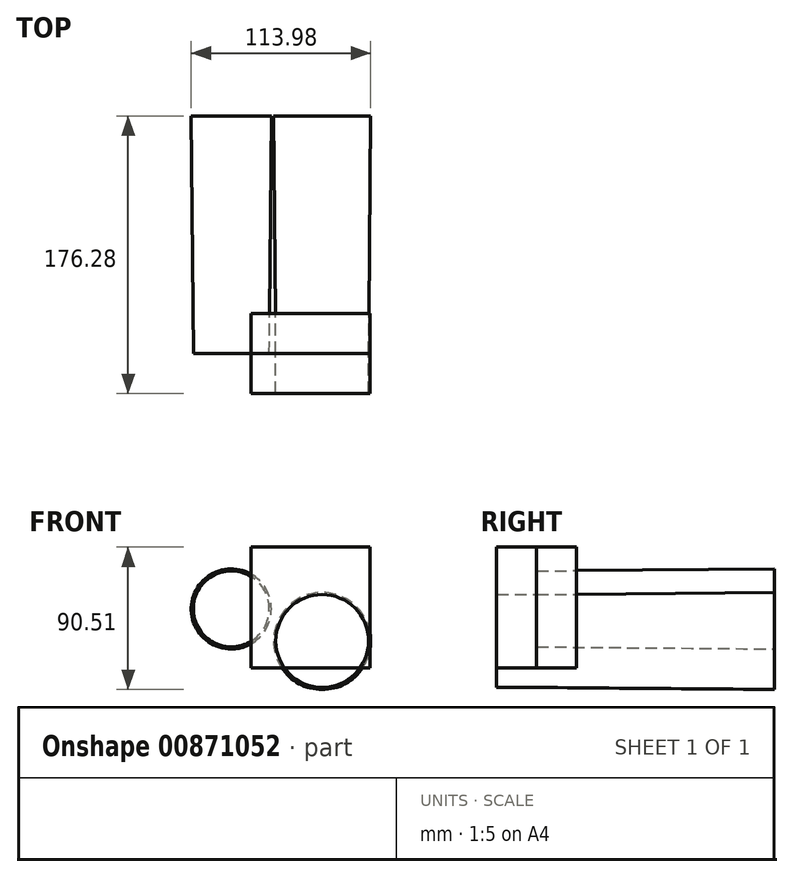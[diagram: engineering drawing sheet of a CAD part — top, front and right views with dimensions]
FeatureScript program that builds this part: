
annotation { "Feature Type Name" : "Feature", "Feature Type Description" : "" }
export const myFeature = defineFeature(function(context is Context, id is Id, definition is map)
    precondition{}
    {
        {
            var Q0;
            Q0=qCreatedBy(makeId("Front.planeOp"),FACE);
            var sketch = newSketch(context, id + "F0", { "sketchPlane" : qUnion([Q0])});
            skCircle(sketch, "E0", {"center": v(-48.02, 37.3) * mm, "radius": 25.42 * mm});
            skCircle(sketch, "E1", {"center": v(9.73, 16.93) * mm, "radius": 30.8 * mm});
            skSolve(sketch);
        }
        {
            var Q0;
            Q0 = qSketchRegion(id + "F0", true);
            extrude(context, id + "F1", {"entities" : qUnion([Q0]), "depth" : 150.88 * mm, "offsetDistance" : 25.4 * mm, "hasDraft" : true, "draftAngle" : .5 * degree, "draftPullDirection" : true});
        }
        {
            var Q0;
            Q0=makeQuery(id+"F1.opExtrude","CAP_FACE",FACE,{"disambiguationData":[OSD([sQuery(id+"F0.wireOp",EDGE,"E1")])],"isStart":false});
            extrude(context, id + "F2", {"entities" : qUnion([Q0]), "operationType" : NewBodyOperationType.ADD, "depth" : 25.4 * mm, "offsetDistance" : 25.4 * mm});
        }
        {
            var Q0;
            Q0=makeQuery(id+"F1.opExtrude","CAP_FACE",FACE,{"disambiguationData":[OSD([sQuery(id+"F0.wireOp",EDGE,"E0")])],"isStart":false});
            var sketch = newSketch(context, id + "F3", { "sketchPlane" : qUnion([Q0])});
            skLineSegment(sketch, "E2.bottom", {"start": v(-35.38, 76.63) * mm, "end": v(40.13, 76.63) * mm});
            skLineSegment(sketch, "E2.top", {"start": v(-35.38, 0) * mm, "end": v(40.13, 0) * mm});
            skLineSegment(sketch, "E2.left", {"start": v(-35.38, 76.63) * mm, "end": v(-35.38, 0) * mm});
            skLineSegment(sketch, "E2.right", {"start": v(40.13, 76.63) * mm, "end": v(40.13, 0) * mm});
            skSolve(sketch);
        }
        {
            var Q0;
            Q0 = qSketchRegion(id + "F3", true);
            extrude(context, id + "F4", {"entities" : qUnion([Q0]), "depth" : 25.4 * mm, "offsetDistance" : 25.4 * mm});
        }
        {
            var Q0;
            Q0=makeQuery(id+"F4.opExtrude","CAP_FACE",FACE,{"disambiguationData":[OSD([sQuery(id+"F3.wireOp",EDGE,"E2.bottom"),sQuery(id+"F3.wireOp",EDGE,"E2.top"),sQuery(id+"F3.wireOp",EDGE,"E2.left"),sQuery(id+"F3.wireOp",EDGE,"E2.right")])],"isStart":true});
            extrude(context, id + "F5", {"entities" : qUnion([Q0]), "depth" : 25.4 * mm, "offsetDistance" : 25.4 * mm});
        }
    });
